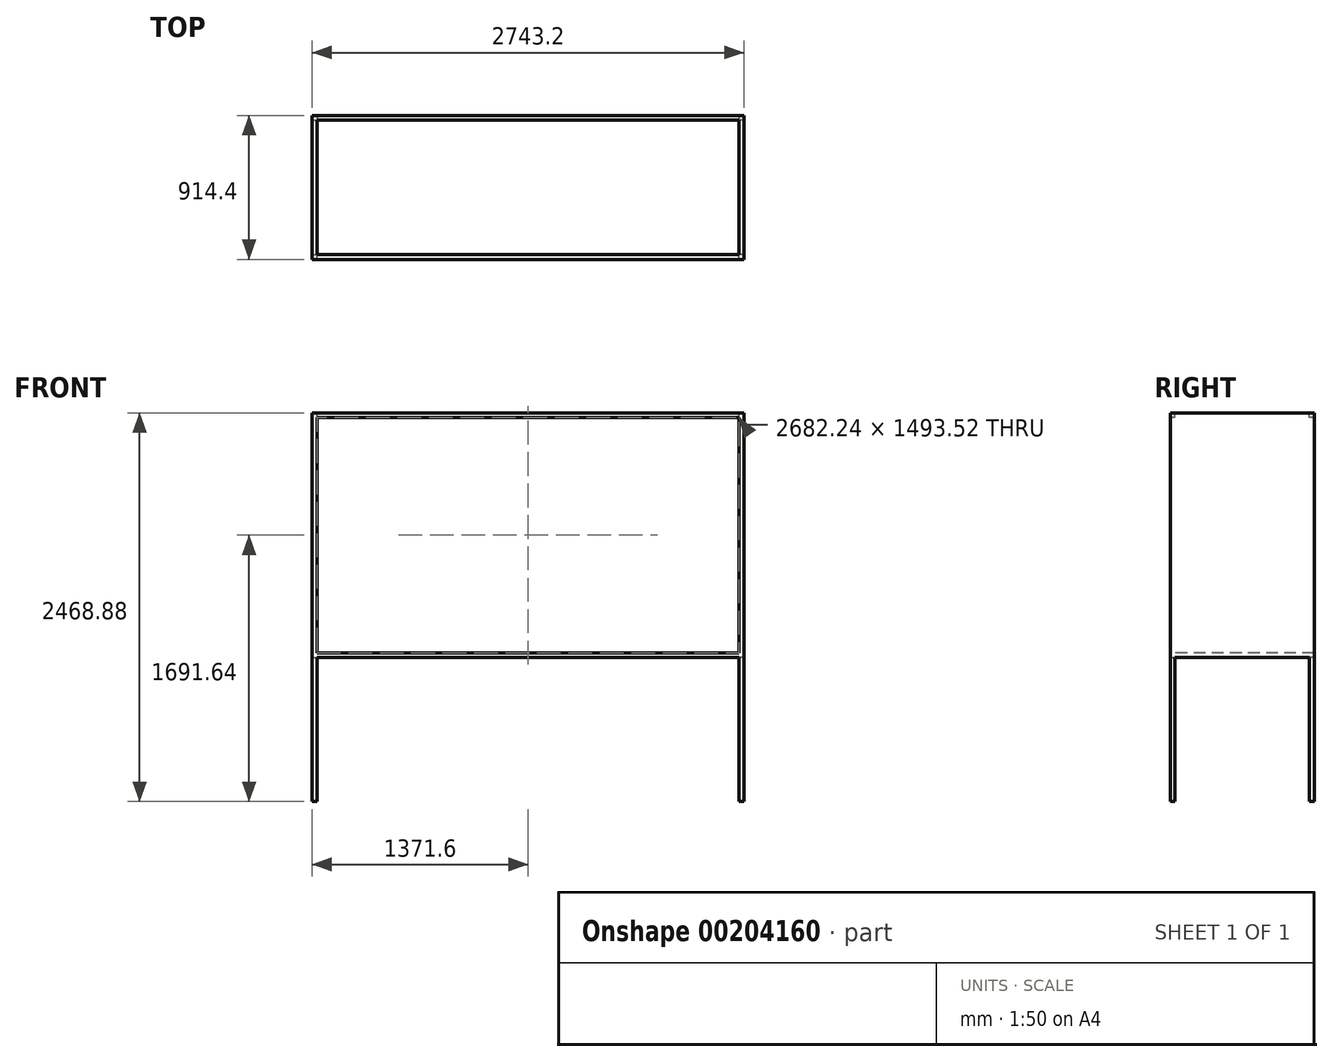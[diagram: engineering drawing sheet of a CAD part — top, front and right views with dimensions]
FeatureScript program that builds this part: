
annotation { "Feature Type Name" : "Feature", "Feature Type Description" : "" }
export const myFeature = defineFeature(function(context is Context, id is Id, definition is map)
    precondition{}
    {
        {
            var Q0;
            Q0=qCreatedBy(makeId("Top.planeOp"),FACE);
            var sketch = newSketch(context, id + "F0", { "sketchPlane" : qUnion([Q0])});
            skLineSegment(sketch, "E0.bottom", {"start": v(0, 0) * mm, "end": v(2743.2, 0) * mm});
            skLineSegment(sketch, "E0.top", {"start": v(0, 914.4) * mm, "end": v(2743.2, 914.4) * mm});
            skLineSegment(sketch, "E0.left", {"start": v(0, 0) * mm, "end": v(0, 914.4) * mm});
            skLineSegment(sketch, "E0.right", {"start": v(2743.2, 0) * mm, "end": v(2743.2, 914.4) * mm});
            skSolve(sketch);
        }
        {
            var Q0;
            Q0=makeQuery(id+"F0.imprint","IMPRINT",FACE,{"disambiguationData":[TD([[makeQuery(id+"F0.imprint","IMPRINT",EDGE,{"derivedFrom":sQuery(id+"F0.wireOp",EDGE,"E0.bottom")}),1.0]])]});
            extrude(context, id + "F1", {"entities" : qUnion([Q0]), "depth" : 30.48 * mm});
        }
        {
            var Q0;
            Q0=makeQuery(id+"F1.opExtrude","CAP_FACE",FACE,{"disambiguationData":[OSD([sQuery(id+"F0.wireOp",EDGE,"E0.bottom"),sQuery(id+"F0.wireOp",EDGE,"E0.top"),sQuery(id+"F0.wireOp",EDGE,"E0.left"),sQuery(id+"F0.wireOp",EDGE,"E0.right")])],"isStart":false});
            var sketch = newSketch(context, id + "F2", { "sketchPlane" : qUnion([Q0])});
            skLineSegment(sketch, "E1.bottom", {"start": v(0, 914.4) * mm, "end": v(2743.2, 914.4) * mm});
            skLineSegment(sketch, "E1.top", {"start": v(0, 0) * mm, "end": v(2743.2, 0) * mm});
            skLineSegment(sketch, "E1.left", {"start": v(0, 914.4) * mm, "end": v(0, 0) * mm});
            skLineSegment(sketch, "E1.right", {"start": v(2743.2, 914.4) * mm, "end": v(2743.2, 0) * mm});
            skSolve(sketch);
        }
        {
            var Q0;
            Q0 = qSketchRegion(id + "F2", true);
            extrude(context, id + "F3", {"entities" : qUnion([Q0]), "operationType" : NewBodyOperationType.ADD, "depth" : 1524 * mm});
        }
        {
            var Q0;
            Q0=makeQuery(id+"F3.opExtrude","CAP_FACE",FACE,{"disambiguationData":[OSD([sQuery(id+"F2.wireOp",EDGE,"E1.bottom"),sQuery(id+"F2.wireOp",EDGE,"E1.top"),sQuery(id+"F2.wireOp",EDGE,"E1.left"),sQuery(id+"F2.wireOp",EDGE,"E1.right")])],"isStart":false});
            var sketch = newSketch(context, id + "F4", { "sketchPlane" : qUnion([Q0])});
            skLineSegment(sketch, "E2.top", {"start": v(30.48, 0) * mm, "end": v(2719.5, 0) * mm});
            skLineSegment(sketch, "E3.bottom", {"start": v(30.48, 883.92) * mm, "end": v(2712.72, 883.92) * mm});
            skLineSegment(sketch, "E3.top", {"start": v(30.48, 30.48) * mm, "end": v(2712.72, 30.48) * mm});
            skLineSegment(sketch, "E3.left", {"start": v(30.48, 883.92) * mm, "end": v(30.48, 30.48) * mm});
            skLineSegment(sketch, "E3.right", {"start": v(2712.72, 883.92) * mm, "end": v(2712.72, 30.48) * mm});
            skSolve(sketch);
        }
        {
            var Q0;
            Q0=makeQuery(id+"F4.imprint","IMPRINT",FACE,{"disambiguationData":[TD([[makeQuery(id+"F4.imprint","IMPRINT",EDGE,{"derivedFrom":sQuery(id+"F4.wireOp",EDGE,"E3.bottom")}),-1.0]])]});
            extrude(context, id + "F5", {"entities" : qUnion([Q0]), "operationType" : NewBodyOperationType.REMOVE, "endBound" : BoundingType.UP_TO_NEXT, "oppositeDirection" : true, "depth" : 1524 * mm});
        }
        {
            var Q0;
            Q0=makeQuery(id+"F3.boolean.opBoolean","MERGE",FACE,{"derivedFrom":[makeQuery(id+"F1.opExtrude","SWEPT_FACE",FACE,{"disambiguationData":[OSD([sQuery(id+"F0.wireOp",EDGE,"E0.bottom")])]}),makeQuery(id+"F3.opExtrude","SWEPT_FACE",FACE,{"disambiguationData":[OSD([sQuery(id+"F2.wireOp",EDGE,"E1.top")])]})]});
            var sketch = newSketch(context, id + "F6", { "sketchPlane" : qUnion([Q0])});
            skLineSegment(sketch, "E4.bottom", {"start": v(30.48, 1524) * mm, "end": v(2712.72, 1524) * mm});
            skLineSegment(sketch, "E4.top", {"start": v(30.48, 30.48) * mm, "end": v(2712.72, 30.48) * mm});
            skLineSegment(sketch, "E4.left", {"start": v(30.48, 1524) * mm, "end": v(30.48, 30.48) * mm});
            skLineSegment(sketch, "E4.right", {"start": v(2712.72, 1524) * mm, "end": v(2712.72, 30.48) * mm});
            skSolve(sketch);
        }
        {
            var Q0;
            Q0=makeQuery(id+"F6.imprint","IMPRINT",FACE,{"disambiguationData":[TD([[makeQuery(id+"F6.imprint","IMPRINT",EDGE,{"derivedFrom":sQuery(id+"F6.wireOp",EDGE,"E4.bottom")}),-1.0]])]});
            extrude(context, id + "F7", {"entities" : qUnion([Q0]), "operationType" : NewBodyOperationType.REMOVE, "oppositeDirection" : true, "depth" : 914.4 * mm});
        }
        {
            var Q0;
            Q0=makeQuery(id+"F7.boolean.opBoolean","SPLIT",FACE,{"disambiguationData":[TD([makeQuery(id+"F7.opExtrude","SWEPT_FACE",FACE,{"disambiguationData":[OSD([sQuery(id+"F6.wireOp",EDGE,"E4.top")])]})])],"derivedFrom":makeQuery(id+"F5.boolean.opBoolean","COPY",FACE,{"derivedFrom":makeQuery(id+"F5.opExtrude","SWEPT_FACE",FACE,{"disambiguationData":[OSD([sQuery(id+"F4.wireOp",EDGE,"E3.bottom")])]})})});
            var sketch = newSketch(context, id + "F8", { "sketchPlane" : qUnion([Q0])});
            skLineSegment(sketch, "E5.bottom", {"start": v(30.48, 30.48) * mm, "end": v(2712.72, 30.48) * mm});
            skLineSegment(sketch, "E5.top", {"start": v(30.48, 0) * mm, "end": v(2712.72, 0) * mm});
            skLineSegment(sketch, "E5.left", {"start": v(30.48, 30.48) * mm, "end": v(30.48, 0) * mm});
            skLineSegment(sketch, "E5.right", {"start": v(2712.72, 30.48) * mm, "end": v(2712.72, 0) * mm});
            skSolve(sketch);
        }
        {
            var Q0;
            Q0 = qSketchRegion(id + "F8", true);
            extrude(context, id + "F9", {"entities" : qUnion([Q0]), "operationType" : NewBodyOperationType.ADD, "endBound" : BoundingType.UP_TO_NEXT, "depth" : 30.48 * mm});
        }
        {
            var Q0;
            Q0=makeQuery(id+"F9.boolean.opBoolean","MERGE",FACE,{"derivedFrom":[makeQuery(id+"F1.opExtrude","CAP_FACE",FACE,{"disambiguationData":[OSD([sQuery(id+"F0.wireOp",EDGE,"E0.bottom"),sQuery(id+"F0.wireOp",EDGE,"E0.top"),sQuery(id+"F0.wireOp",EDGE,"E0.left"),sQuery(id+"F0.wireOp",EDGE,"E0.right")])],"isStart":true}),makeQuery(id+"F9.opExtrude","SWEPT_FACE",FACE,{"disambiguationData":[OSD([sQuery(id+"F8.wireOp",EDGE,"E5.top")])]})]});
            var sketch = newSketch(context, id + "F10", { "sketchPlane" : qUnion([Q0])});
            skLineSegment(sketch, "E6.bottom", {"start": v(0, 0) * mm, "end": v(30.48, 0) * mm});
            skLineSegment(sketch, "E6.top", {"start": v(0, -30.48) * mm, "end": v(30.48, -30.48) * mm});
            skLineSegment(sketch, "E6.left", {"start": v(0, 0) * mm, "end": v(0, -30.48) * mm});
            skLineSegment(sketch, "E6.right", {"start": v(30.48, 0) * mm, "end": v(30.48, -30.48) * mm});
            skLineSegment(sketch, "E7.bottom", {"start": v(0, -914.4) * mm, "end": v(30.48, -914.4) * mm});
            skLineSegment(sketch, "E7.top", {"start": v(0, -883.92) * mm, "end": v(30.48, -883.92) * mm});
            skLineSegment(sketch, "E7.left", {"start": v(0, -914.4) * mm, "end": v(0, -883.92) * mm});
            skLineSegment(sketch, "E7.right", {"start": v(30.48, -914.4) * mm, "end": v(30.48, -883.92) * mm});
            skLineSegment(sketch, "E8.bottom", {"start": v(2743.2, 0) * mm, "end": v(2712.72, 0) * mm});
            skLineSegment(sketch, "E8.top", {"start": v(2743.2, -30.48) * mm, "end": v(2712.72, -30.48) * mm});
            skLineSegment(sketch, "E8.left", {"start": v(2743.2, 0) * mm, "end": v(2743.2, -30.48) * mm});
            skLineSegment(sketch, "E8.right", {"start": v(2712.72, 0) * mm, "end": v(2712.72, -30.48) * mm});
            skLineSegment(sketch, "E9.bottom", {"start": v(2743.2, -914.4) * mm, "end": v(2712.72, -914.4) * mm});
            skLineSegment(sketch, "E9.top", {"start": v(2743.2, -883.92) * mm, "end": v(2712.72, -883.92) * mm});
            skLineSegment(sketch, "E9.left", {"start": v(2743.2, -914.4) * mm, "end": v(2743.2, -883.92) * mm});
            skLineSegment(sketch, "E9.right", {"start": v(2712.72, -914.4) * mm, "end": v(2712.72, -883.92) * mm});
            skSolve(sketch);
        }
        {
            var Q0;
            Q0 = qSketchRegion(id + "F10", true);
            extrude(context, id + "F11", {"entities" : qUnion([Q0]), "operationType" : NewBodyOperationType.ADD, "depth" : 914.4 * mm});
        }
    });
